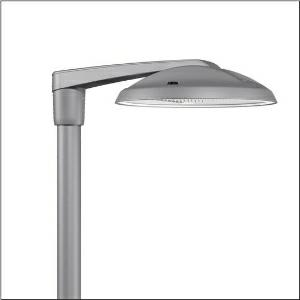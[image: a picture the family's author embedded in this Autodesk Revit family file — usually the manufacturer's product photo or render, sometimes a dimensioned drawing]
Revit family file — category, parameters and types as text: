
# Revit family: dl_r__50_iq_mini___st1_0a_5xa248d31v08ne_16c2
name_source: partatom
category: Lighting Fixtures
units: mm (PartAtom-declared; Revit-internal decimal feet)

## family parameters
Cut with Voids When Loaded = No
Host = Face
Light Source = No
Part Type = Normal
Room Calculation Point = No
Round Connector Dimension = Use Diameter
Shared = No

## types (1)
- --- (1 x LED, 17900 lm, 110.1 W, 3000K)
    Apparent Load = 110 VA
    CIE Flux Codes = 37 72 97 100 100
    Color Rendering = 70
    Color Temperature = 3000K
    Default Elevation = 1800 mm
    Description = DL® 50 iQ mini, mast luminaire, primary light control with lens, of PMMA, primary optical cover: cover, of toughened safety glass, transparent, light distribution: ST1.0a, light emission: direct distribution, primary light characteristic: asymmetric, installation type: post-top, side-entry, LED, High Power LED, rated luminous flux: 17.900lm, luminous efficacy: 163lm/W, light colour: 730, colour temperature: 3000K, control gear: iQ-Street Remote, D4i with power reduction, control: optimised constant luminous flux control (CLO 2.0), Desk-Remote (wireless, voltage-free reading and setting of iQ features in the workshop via application-optimized NFC function/RFID function), Light-Fading, Smart-Wire, Night-Set, Lumen-Switch, Temp-Guard, Auto-Match, Street-Remote, pre-setting: logarithmic dimming characteristic, mains connection: 230..240V, AC, 50/60Hz, connection cable pre-assembled, cable length: 10,5m, start of lifetime: 110W, end of service life: 116W, reduction: 50W, luminaire housing, of diecast aluminium, powder-coated, Siteco® metallic grey (DB 702S), inclination adjustable: 0°, 5°, 10° (post-top) | 0°, -5°, -10°, -15° (side-entry), please order mast post-top element or mast side-entry element separately, diameter: 500mm, height: 115mm, post-top: for spigot size d x l = 76 x 100mm; with reducer (optional accessory) 60 x 100mm | side-entry: for spigot size d x l = 60 x 100mm; with reducer (optional accessory) 42 x 100mm, mounting height: 4..6m, Smart Interface above, protection rating (complete): IP66, insulation class (complete): insulation class II (safety insulation), certification: CE, ENEC, ENEC+, VDE, impact resistance: IK08, permissible operating ambient temperature for outdoor applications: -25..+40°C, standard-compliant lighting for roads and squares, packaging unit: 1 piece

Light Distribution: ST1.0a
    Height = 115 mm
    Lamp = 1 x LED
    Lamp Light Flux = 17900 lm
    Lamp Power = 110.1 W
    Lamp count = 1
    Length = 500 mm
    Luminous efficacy = 163 lm/W
    Manufacturer = Siteco
    ModVariant = No
    Model = 5XA248D31V08NE
    Number of Poles = 1
    OnlyDefault = Yes
    Power Factor = 1
    Product Name = DL® 50 iQ mini | ST1.0a
    Product group = mast luminaire | pylon top
    ProductGroupID = 6100
    Protection Class = Protection class II
    Protection Degree = IP 66
    RLX_Detail_Level = 1
    RLX_Emergency_Light_Flux = 0 lm
    RLX_Emergency_Type = 0
    RLX_Emergency_Type_DB = No
    RlxData = <blob elided: 106869 chars, md5=489f31b3>
    Socket = socket
    Standby Power = 0 W
    System Light Flux = 17900 lm
    System Power = 110 W
    Type Comments = factory setting: luminous flux: 100 % | dim-lin: 254 | 601 mA
    Type Image = l_1251788.jpg
    URL = http://relux.com
    VarID = @adj_086699
    Voltage = 0 V
    Weight = 0.00 kg
    Width = 0 mm  [stored 0 ft]

note: [stored X ft] marks values corroborated as IEEE doubles in the binary element streams (Revit-internal decimal feet)

## geometry (parser evidence)
native form markers: Blend x4, Sweep x10
no freeform markers — native parametric forms only
